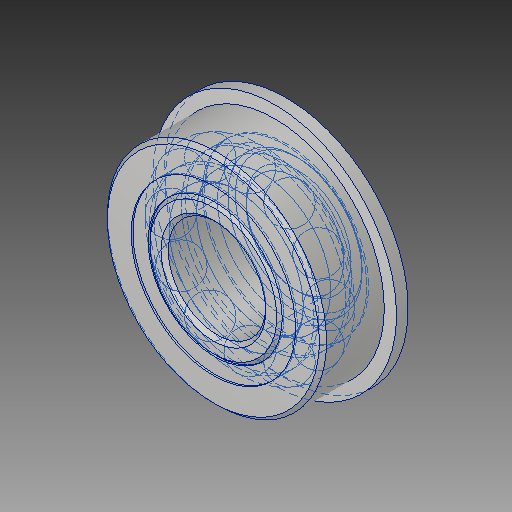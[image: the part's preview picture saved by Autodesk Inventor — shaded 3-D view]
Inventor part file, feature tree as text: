
AUTODESK INVENTOR PART (.ipt)
format: ipt  version: 2019 (Build 230136000, 136)  size: 648,192 bytes
history: native  units: in
note: dims shown in document units (in); Inventor stores cm internally (conversion verified against a paired STEP export)
features: other x11, revolve x5
ambient origin geometry x8: Origin, YZ Plane, XZ Plane, XY Plane, X Axis, Y Axis, Z Axis, Center Point
bodies: Solid1 (feature_tree), Solid2 (feature_tree), Solid3 (feature_tree), Solid4 (feature_tree), Solid5 (feature_tree), Solid6 (feature_tree), Solid7 (feature_tree), Solid8 (feature_tree), Solid9 (feature_tree), Solid10 (feature_tree), Solid11 (feature_tree), Solid12 (feature_tree), Solid13 (feature_tree), Solid14 (feature_tree), Solid15 (feature_tree), Solid16 (feature_tree)
feature tree (16):
  revolve  "Revolve3"  [1 undecoded]
  revolve  "Revolve4"  [1 undecoded]
  other  "CirPattern1[1]"
  other  "CirPattern1[2]"
  other  "CirPattern1[3]"
  other  "CirPattern1[4]"
  other  "CirPattern1[5]"
  other  "CirPattern1[6]"
  other  "CirPattern1[7]"
  other  "CirPattern1[8]"
  other  "CirPattern1[9]"
  other  "CirPattern1[10]"
  other  "CirPattern1[11]"
  revolve  "Revolve5[1]"  [1 undecoded]
  revolve  "Revolve5[2]"  [1 undecoded]
  revolve  "Revolve6"  [1 undecoded]
note: 5 required parameter values undecoded (feature->parameter linkage not recoverable at this tier; creation-order binding heuristic only, values carry confidence <= 0.55)
